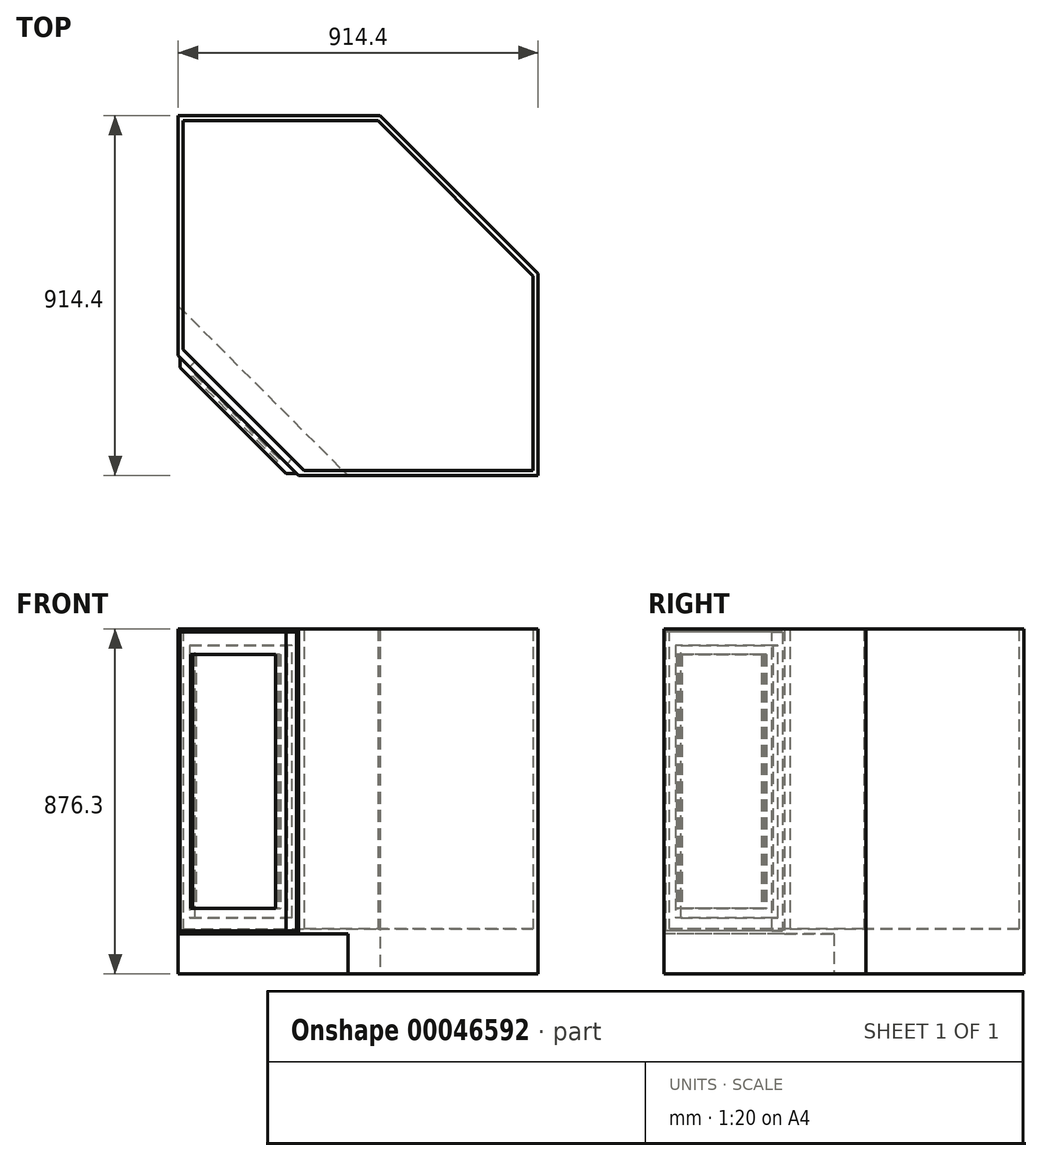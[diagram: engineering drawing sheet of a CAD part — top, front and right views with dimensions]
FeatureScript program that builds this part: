
annotation { "Feature Type Name" : "Feature", "Feature Type Description" : "" }
export const myFeature = defineFeature(function(context is Context, id is Id, definition is map)
    precondition{}
    {
        {
            var Q0;
            Q0=qCreatedBy(makeId("Top.planeOp"),FACE);
            var sketch = newSketch(context, id + "F0", { "sketchPlane" : qUnion([Q0])});
            skLineSegment(sketch, "E0.bottom", {"start": v(-457.2, 457.2) * mm, "end": v(457.2, 457.2) * mm, "construction": true});
            skLineSegment(sketch, "E0.top", {"start": v(-457.2, -457.2) * mm, "end": v(457.2, -457.2) * mm, "construction": true});
            skLineSegment(sketch, "E0.left", {"start": v(-457.2, 457.2) * mm, "end": v(-457.2, -457.2) * mm, "construction": true});
            skLineSegment(sketch, "E0.right", {"start": v(457.2, 457.2) * mm, "end": v(457.2, -457.2) * mm, "construction": true});
            skLineSegment(sketch, "E1", {"start": v(-457.2, 457.2) * mm, "end": v(457.2, -457.2) * mm, "construction": true});
            skLineSegment(sketch, "E2", {"start": v(-457.2, -151.87) * mm, "end": v(-151.87, -457.2) * mm, "construction": true});
            skLineSegment(sketch, "E3", {"start": v(55.33, 457.2) * mm, "end": v(457.2, 55.33) * mm, "construction": true});
            skSolve(sketch);
        }
        {
            var Q0;
            Q0=qCreatedBy(makeId("Top.planeOp"),FACE);
            var sketch = newSketch(context, id + "F1", { "sketchPlane" : qUnion([Q0])});
            skLineSegment(sketch, "E4", {"start": v(-457.2, -151.87) * mm, "end": v(-151.87, -457.2) * mm});
            skLineSegment(sketch, "E5", {"start": v(-457.2, -151.87) * mm, "end": v(-457.2, -124.93) * mm});
            skLineSegment(sketch, "E6", {"start": v(-151.87, -457.2) * mm, "end": v(-124.93, -457.2) * mm});
            skLineSegment(sketch, "E7", {"start": v(-457.2, -124.93) * mm, "end": v(-124.93, -457.2) * mm});
            skLineSegment(sketch, "E8", {"start": v(-457.2, -124.93) * mm, "end": v(-457.2, 457.2) * mm});
            skLineSegment(sketch, "E9", {"start": v(-124.93, -457.2) * mm, "end": v(457.2, -457.2) * mm});
            skLineSegment(sketch, "E10", {"start": v(457.2, -457.2) * mm, "end": v(457.2, 55.33) * mm});
            skLineSegment(sketch, "E11", {"start": v(-457.2, 457.2) * mm, "end": v(55.33, 457.2) * mm});
            skLineSegment(sketch, "E12", {"start": v(55.33, 457.2) * mm, "end": v(457.2, 55.33) * mm});
            skLineSegment(sketch, "E13", {"start": v(-444.5, -137.63) * mm, "end": v(-444.5, 444.5) * mm});
            skLineSegment(sketch, "E14", {"start": v(-444.5, 444.5) * mm, "end": v(50.07, 444.5) * mm});
            skLineSegment(sketch, "E15", {"start": v(50.07, 444.5) * mm, "end": v(444.5, 50.07) * mm});
            skLineSegment(sketch, "E16", {"start": v(444.5, 50.07) * mm, "end": v(444.5, -444.5) * mm});
            skLineSegment(sketch, "E17", {"start": v(444.5, -444.5) * mm, "end": v(-137.63, -444.5) * mm});
            skSolve(sketch);
        }
        {
            var Q0;
            Q0=makeQuery(id+"F1.imprint","IMPRINT",FACE,{"disambiguationData":[TD([[makeQuery(id+"F1.imprint","IMPRINT",EDGE,{"derivedFrom":sQuery(id+"F1.wireOp",EDGE,"E4")}),1.0]])]});
            var Q1;
            {var subQ1=sQuery(id+"F1.wireOp",EDGE,"E8");Q1=makeQuery(id+"F1.imprint","IMPRINT",FACE,{"disambiguationData":[TD([[makeQuery(id+"F1.imprint","IMPRINT",EDGE,{"derivedFrom":subQ1}),-1.0]])]});}
            extrude(context, id + "F2", {"entities" : qUnion([Q0, Q1]), "depth" : 774.7 * mm});
        }
        {
            var Q0;
            Q0=makeQuery(id+"F2.opExtrude","CAP_FACE",FACE,{"disambiguationData":[OSD([sQuery(id+"F1.wireOp",EDGE,"E4"),sQuery(id+"F1.wireOp",EDGE,"E5"),sQuery(id+"F1.wireOp",EDGE,"E6"),sQuery(id+"F1.wireOp",EDGE,"E7"),sQuery(id+"F1.wireOp",EDGE,"E8"),sQuery(id+"F1.wireOp",EDGE,"E9"),sQuery(id+"F1.wireOp",EDGE,"E10"),sQuery(id+"F1.wireOp",EDGE,"E11"),sQuery(id+"F1.wireOp",EDGE,"E12"),sQuery(id+"F1.wireOp",EDGE,"E13"),sQuery(id+"F1.wireOp",EDGE,"E14"),sQuery(id+"F1.wireOp",EDGE,"E15"),sQuery(id+"F1.wireOp",EDGE,"E16"),sQuery(id+"F1.wireOp",EDGE,"E17")])],"isStart":true});
            var Q1;
            {var subQ0=sQuery(id+"F1.wireOp",EDGE,"E13");Q1=makeQuery(id+"F1.imprint","IMPRINT",FACE,{"disambiguationData":[TD([[makeQuery(id+"F1.imprint","IMPRINT",EDGE,{"derivedFrom":subQ0}),-1.0]])]});}
            var Q2;
            Q2=sQuery(id+"F1.wireOp",EDGE,"E4");
            var Q3;
            Q3=sQuery(id+"F1.wireOp",EDGE,"E6");
            var Q4;
            Q4=sQuery(id+"F1.wireOp",EDGE,"E9");
            var Q5;
            Q5=sQuery(id+"F1.wireOp",EDGE,"E5");
            var Q6;
            Q6=sQuery(id+"F1.wireOp",EDGE,"E8");
            var Q7;
            Q7=sQuery(id+"F1.wireOp",EDGE,"E11");
            var Q8;
            Q8=sQuery(id+"F1.wireOp",EDGE,"E12");
            var Q9;
            Q9=sQuery(id+"F1.wireOp",EDGE,"E10");
            extrude(context, id + "F3", {"entities" : qUnion([Q0, Q1]), "operationType" : NewBodyOperationType.ADD, "surfaceEntities" : qUnion([Q2, Q3, Q4, Q5, Q6, Q7, Q8, Q9]), "depth" : 101.6 * mm, "hasSecondDirection" : true, "secondDirectionOppositeDirection" : true, "secondDirectionDepth" : 12.7 * mm});
        }
        {
            var Q0;
            {var subQ0=sQuery(id+"F1.wireOp",EDGE,"E17");var subQ1=sQuery(id+"F1.wireOp",EDGE,"E16");var subQ2=sQuery(id+"F1.wireOp",EDGE,"E15");var subQ3=sQuery(id+"F1.wireOp",EDGE,"E14");var subQ4=sQuery(id+"F1.wireOp",EDGE,"E13");var subQ5=sQuery(id+"F1.wireOp",EDGE,"E7");Q0=makeQuery(id+"F3.boolean.opBoolean","MERGE",FACE,{"derivedFrom":[makeQuery(id+"F3.opExtrude","CAP_FACE",FACE,{"disambiguationData":[OSD([subQ5,subQ4,subQ3,subQ2,subQ1,subQ0])],"isStart":false}),makeQuery(id+"F3.opExtrude","CAP_FACE",FACE,{"disambiguationData":[OSD([sQuery(id+"F1.wireOp",EDGE,"E4"),sQuery(id+"F1.wireOp",EDGE,"E5"),sQuery(id+"F1.wireOp",EDGE,"E6"),subQ5,sQuery(id+"F1.wireOp",EDGE,"E8"),sQuery(id+"F1.wireOp",EDGE,"E9"),sQuery(id+"F1.wireOp",EDGE,"E10"),sQuery(id+"F1.wireOp",EDGE,"E11"),sQuery(id+"F1.wireOp",EDGE,"E12"),subQ4,subQ3,subQ2,subQ1,subQ0])],"isStart":false})]});}
            var sketch = newSketch(context, id + "F4", { "sketchPlane" : qUnion([Q0])});
            skLineSegment(sketch, "E18", {"start": v(-151.87, 457.2) * mm, "end": v(-457.2, 151.87) * mm});
            skLineSegment(sketch, "E19", {"start": v(-457.2, 151.87) * mm, "end": v(-457.2, 26.15) * mm});
            skLineSegment(sketch, "E20", {"start": v(-151.87, 457.2) * mm, "end": v(-26.15, 457.2) * mm});
            skLineSegment(sketch, "E21", {"start": v(-457.2, 26.15) * mm, "end": v(-26.15, 457.2) * mm});
            skSolve(sketch);
        }
        {
            var Q0;
            Q0=qSketchRegion(id+"F4",true);
            extrude(context, id + "F5", {"entities" : qUnion([Q0]), "operationType" : NewBodyOperationType.REMOVE, "oppositeDirection" : true, "depth" : 101.6 * mm});
        }
        {
            var Q0;
            {var subQ0=sQuery(id+"F1.wireOp",EDGE,"E4");Q0=makeQuery(id+"F3.boolean.opBoolean","MERGE",FACE,{"derivedFrom":[makeQuery(id+"F2.opExtrude","SWEPT_FACE",FACE,{"disambiguationData":[OSD([subQ0])]}),makeQuery(id+"F3.opExtrude","SWEPT_FACE",FACE,{"disambiguationData":[OSD([subQ0])]})]});}
            var sketch = newSketch(context, id + "F6", { "sketchPlane" : qUnion([Q0])});
            skLineSegment(sketch, "E22.bottom", {"start": v(-174.62, 733.42) * mm, "end": v(174.62, 733.42) * mm});
            skLineSegment(sketch, "E22.top", {"start": v(-174.62, 41.28) * mm, "end": v(174.63, 41.28) * mm});
            skLineSegment(sketch, "E22.left", {"start": v(-174.62, 733.42) * mm, "end": v(-174.62, 41.28) * mm});
            skLineSegment(sketch, "E22.right", {"start": v(174.62, 733.42) * mm, "end": v(174.63, 41.28) * mm});
            skSolve(sketch);
        }
        {
            var Q0;
            Q0=qSketchRegion(id+"F6",true);
            var Q1;
            Q1=makeQuery(id+"F6.imprint","IMPRINT",FACE,{"disambiguationData":[TD([[makeQuery(id+"F6.imprint","IMPRINT",EDGE,{"derivedFrom":sQuery(id+"F6.wireOp",EDGE,"E22.bottom")}),-1.0]])]});
            extrude(context, id + "F7", {"entities" : qUnion([Q0, Q1]), "operationType" : NewBodyOperationType.REMOVE, "oppositeDirection" : true, "depth" : 25.4 * mm});
        }
        {
            var Q0;
            {var subQ0=sQuery(id+"F1.wireOp",EDGE,"E4");Q0=makeQuery(id+"F3.boolean.opBoolean","MERGE",FACE,{"derivedFrom":[makeQuery(id+"F2.opExtrude","SWEPT_FACE",FACE,{"disambiguationData":[OSD([subQ0])]}),makeQuery(id+"F3.opExtrude","SWEPT_FACE",FACE,{"disambiguationData":[OSD([subQ0])]})]});}
            var sketch = newSketch(context, id + "F8", { "sketchPlane" : qUnion([Q0])});
            skLineSegment(sketch, "E23.bottom", {"start": v(-209.55, 766.76) * mm, "end": v(209.55, 766.76) * mm});
            skLineSegment(sketch, "E23.top", {"start": v(-209.55, 7.94) * mm, "end": v(209.55, 7.94) * mm});
            skLineSegment(sketch, "E23.left", {"start": v(-209.55, 766.76) * mm, "end": v(-209.55, 7.94) * mm});
            skLineSegment(sketch, "E23.right", {"start": v(209.55, 766.76) * mm, "end": v(209.55, 7.94) * mm});
            skLineSegment(sketch, "E24.bottom", {"start": v(-152.4, 709.61) * mm, "end": v(152.4, 709.61) * mm});
            skLineSegment(sketch, "E24.top", {"start": v(-152.4, 65.09) * mm, "end": v(152.4, 65.09) * mm});
            skLineSegment(sketch, "E24.left", {"start": v(-152.4, 709.61) * mm, "end": v(-152.4, 65.09) * mm});
            skLineSegment(sketch, "E24.right", {"start": v(152.4, 709.61) * mm, "end": v(152.4, 65.09) * mm});
            skSolve(sketch);
        }
        {
            var Q0;
            Q0=qSketchRegion(id+"F8",true);
            extrude(context, id + "F9", {"entities" : qUnion([Q0]), "depth" : 19.05 * mm});
        }
        {
            var Q0;
            Q0=makeQuery(id+"F9.opExtrude","SWEPT_FACE",FACE,{"disambiguationData":[OSD([sQuery(id+"F8.wireOp",EDGE,"E23.bottom")])]});
            var sketch = newSketch(context, id + "F10", { "sketchPlane" : qUnion([Q0])});
            skLineSegment(sketch, "E25", {"start": v(-156.36, -452.7) * mm, "end": v(-183.3, -452.7) * mm});
            skLineSegment(sketch, "E26", {"start": v(-156.36, -452.7) * mm, "end": v(-169.83, -466.18) * mm});
            skLineSegment(sketch, "E27", {"start": v(-169.83, -466.18) * mm, "end": v(-183.3, -452.7) * mm});
            skLineSegment(sketch, "E28", {"start": v(-452.7, -156.36) * mm, "end": v(-466.18, -169.83) * mm});
            skLineSegment(sketch, "E29", {"start": v(-466.18, -169.83) * mm, "end": v(-452.7, -183.3) * mm});
            skLineSegment(sketch, "E30", {"start": v(-452.7, -183.3) * mm, "end": v(-452.7, -156.36) * mm});
            skSolve(sketch);
        }
        {
            var Q0;
            Q0=qSketchRegion(id+"F10",true);
            extrude(context, id + "F11", {"entities" : qUnion([Q0]), "operationType" : NewBodyOperationType.REMOVE, "endBound" : BoundingType.THROUGH_ALL, "oppositeDirection" : true, "depth" : 25.4 * mm});
        }
        {
            var Q0;
            Q0=makeQuery(id+"F9.opExtrude","SWEPT_FACE",FACE,{"disambiguationData":[OSD([sQuery(id+"F8.wireOp",EDGE,"E24.top")])]});
            var sketch = newSketch(context, id + "F12", { "sketchPlane" : qUnion([Q0])});
            skLineSegment(sketch, "E31", {"start": v(-415.67, -200.14) * mm, "end": v(-420.16, -204.63) * mm});
            skLineSegment(sketch, "E32", {"start": v(-200.14, -415.67) * mm, "end": v(-204.63, -420.16) * mm});
            skLineSegment(sketch, "E33", {"start": v(-200.14, -415.67) * mm, "end": v(-415.67, -200.14) * mm});
            skLineSegment(sketch, "E34", {"start": v(-420.16, -204.63) * mm, "end": v(-204.63, -420.16) * mm});
            skSolve(sketch);
        }
        {
            var Q0;
            Q0=qSketchRegion(id+"F12",true);
            extrude(context, id + "F13", {"entities" : qUnion([Q0]), "operationType" : NewBodyOperationType.ADD, "endBound" : BoundingType.UP_TO_NEXT, "depth" : 25.4 * mm});
        }
    });
